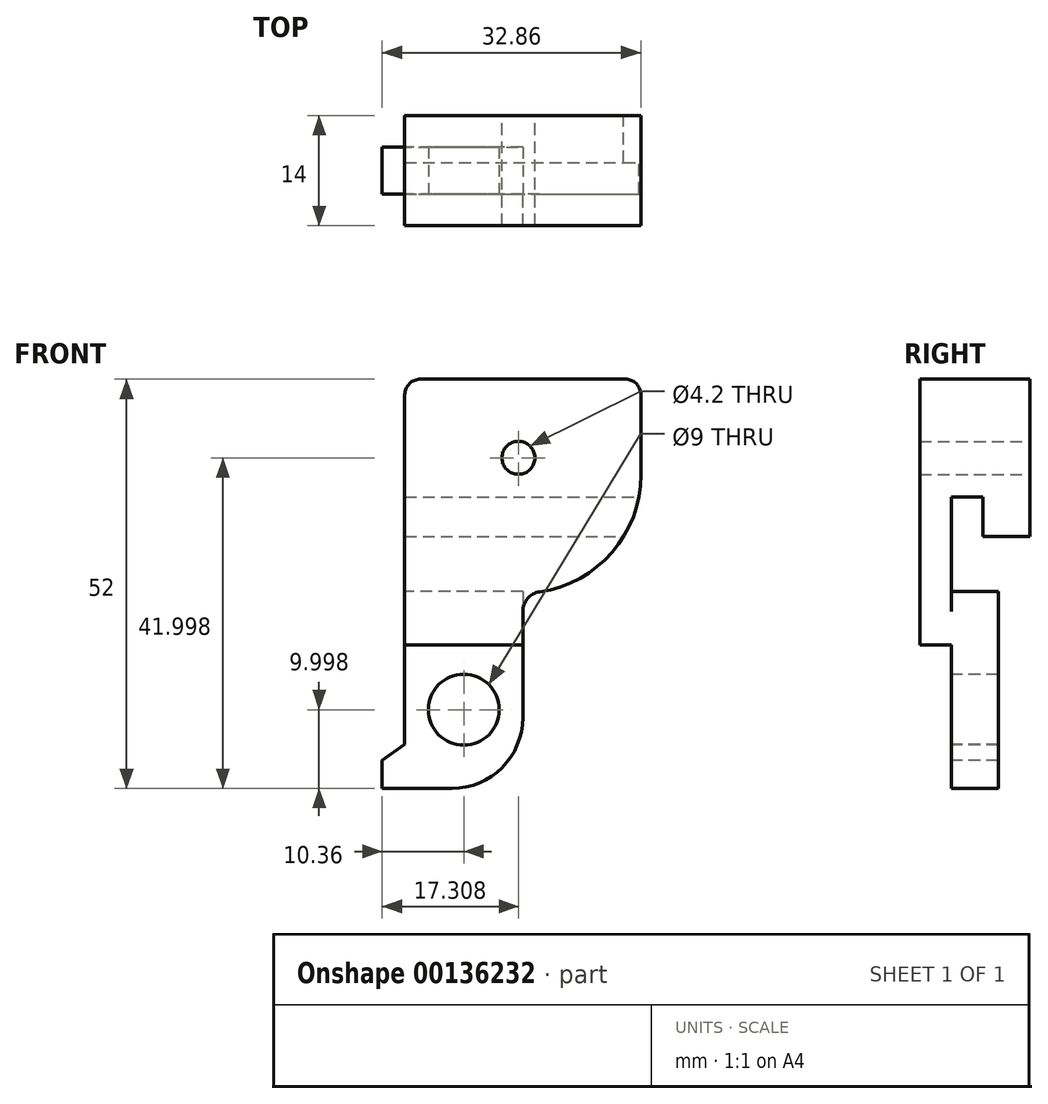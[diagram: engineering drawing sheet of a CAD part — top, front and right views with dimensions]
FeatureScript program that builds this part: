
annotation { "Feature Type Name" : "Feature", "Feature Type Description" : "" }
export const myFeature = defineFeature(function(context is Context, id is Id, definition is map)
    precondition{}
    {
        {
            var Q0;
            Q0=qCreatedBy(makeId("Front.planeOp"),FACE);
            var sketch = newSketch(context, id + "F0", { "sketchPlane" : qUnion([Q0])});
            skLineSegment(sketch, "E0.bottom", {"start": v(-22.02, 18.76) * mm, "end": v(7.98, 18.76) * mm});
            skLineSegment(sketch, "E0.top", {"start": v(-7.02, -8.24) * mm, "end": v(7.98, -8.24) * mm});
            skLineSegment(sketch, "E0.left", {"start": v(-22.02, 18.76) * mm, "end": v(-22.02, -8.24) * mm});
            skLineSegment(sketch, "E0.right", {"start": v(7.98, 18.76) * mm, "end": v(7.98, -8.24) * mm});
            skLineSegment(sketch, "E1.bottom", {"start": v(-22.02, 13.76) * mm, "end": v(7.98, 13.76) * mm});
            skLineSegment(sketch, "E1.top", {"start": v(-22.02, 3.76) * mm, "end": v(7.98, 3.76) * mm});
            skLineSegment(sketch, "E1.left", {"start": v(-22.02, 13.76) * mm, "end": v(-22.02, 3.76) * mm});
            skLineSegment(sketch, "E1.right", {"start": v(7.98, 13.76) * mm, "end": v(7.98, 3.76) * mm});
            skLineSegment(sketch, "E2.bottom", {"start": v(-22.02, 3.76) * mm, "end": v(-7.02, 3.76) * mm});
            skLineSegment(sketch, "E2.top", {"start": v(-22.02, -33.24) * mm, "end": v(-7.02, -33.24) * mm});
            skLineSegment(sketch, "E2.left", {"start": v(-22.02, 3.76) * mm, "end": v(-22.02, -33.24) * mm});
            skLineSegment(sketch, "E2.right", {"start": v(-7.02, -8.24) * mm, "end": v(-7.02, -33.24) * mm});
            skCircle(sketch, "E3", {"center": v(-7.57, 8.76) * mm, "radius": 2.1 * mm});
            skCircle(sketch, "E4", {"center": v(-14.52, -23.24) * mm, "radius": 4.5 * mm});
            skLineSegment(sketch, "E5", {"start": v(-7.02, -8.24) * mm, "end": v(-22.02, -8.24) * mm});
            skLineSegment(sketch, "E6", {"start": v(-7.02, -15) * mm, "end": v(-22.02, -15) * mm});
            skLineSegment(sketch, "E7", {"start": v(-22.02, -33.24) * mm, "end": v(-24.88, -33.24) * mm});
            skLineSegment(sketch, "E8", {"start": v(-24.88, -33.24) * mm, "end": v(-24.88, -29.67) * mm});
            skLineSegment(sketch, "E9", {"start": v(-24.88, -29.67) * mm, "end": v(-22.02, -27.65) * mm});
            skSolve(sketch);
        }
        {
            var Q0;
            {var subQ0=sQuery(id+"F0.wireOp",EDGE,"E0.bottom");Q0=makeQuery(id+"F0.imprint","IMPRINT",FACE,{"disambiguationData":[TD([[makeQuery(id+"F0.imprint","IMPRINT",EDGE,{"derivedFrom":subQ0}),-1.0]])]});}
            var Q1;
            Q1=makeQuery(id+"F0.imprint","IMPRINT",FACE,{"disambiguationData":[TD([[makeQuery(id+"F0.imprint","IMPRINT",EDGE,{"derivedFrom":sQuery(id+"F0.wireOp",EDGE,"E1.bottom")}),-1.0]])]});
            var Q2;
            {var subQ3=sQuery(id+"F0.wireOp",EDGE,"E0.top");Q2=makeQuery(id+"F0.imprint","IMPRINT",FACE,{"disambiguationData":[TD([[makeQuery(id+"F0.imprint","IMPRINT",EDGE,{"derivedFrom":subQ3}),1.0]])]});}
            var Q3;
            {var subQ0=sQuery(id+"F0.wireOp",EDGE,"E5");Q3=makeQuery(id+"F0.imprint","IMPRINT",FACE,{"disambiguationData":[TD([[makeQuery(id+"F0.imprint","IMPRINT",EDGE,{"derivedFrom":subQ0}),1.0]])]});}
            extrude(context, id + "F1", {"entities" : qUnion([Q0, Q1, Q2, Q3]), "depth" : 4 * mm});
        }
        {
            var Q0;
            Q0=makeQuery(id+"F0.imprint","IMPRINT",FACE,{"disambiguationData":[TD([[makeQuery(id+"F0.imprint","IMPRINT",EDGE,{"derivedFrom":sQuery(id+"F0.wireOp",EDGE,"E1.bottom")}),-1.0]])]});
            extrude(context, id + "F2", {"entities" : qUnion([Q0]), "operationType" : NewBodyOperationType.ADD, "oppositeDirection" : true, "depth" : 4 * mm});
        }
        {
            var Q0;
            Q0=makeQuery(id+"F2.opExtrude","CAP_FACE",FACE,{"disambiguationData":[OSD([sQuery(id+"F0.wireOp",EDGE,"E1.bottom"),sQuery(id+"F0.wireOp",EDGE,"E1.top"),sQuery(id+"F0.wireOp",EDGE,"E1.left"),sQuery(id+"F0.wireOp",EDGE,"E1.right"),sQuery(id+"F0.wireOp",EDGE,"E2.bottom"),sQuery(id+"F0.wireOp",EDGE,"E3")])],"isStart":false});
            extrude(context, id + "F3", {"entities" : qUnion([Q0]), "depth" : 6 * mm});
        }
        {
            var Q0;
            Q0=makeQuery(id+"F3.opExtrude","SWEPT_FACE",FACE,{"disambiguationData":[OSD([sQuery(id+"F0.wireOp",EDGE,"E1.top"),sQuery(id+"F0.wireOp",EDGE,"E2.bottom")])]});
            extrude(context, id + "F4", {"entities" : qUnion([Q0]), "operationType" : NewBodyOperationType.ADD, "depth" : 5 * mm});
        }
        {
            var Q0;
            {var subQ0=sQuery(id+"F0.wireOp",EDGE,"E5");Q0=makeQuery(id+"F0.imprint","IMPRINT",FACE,{"disambiguationData":[TD([[makeQuery(id+"F0.imprint","IMPRINT",EDGE,{"derivedFrom":subQ0}),1.0]])]});}
            var Q1;
            {var subQ1=sQuery(id+"F0.wireOp",EDGE,"E2.top");Q1=makeQuery(id+"F0.imprint","IMPRINT",FACE,{"disambiguationData":[TD([[makeQuery(id+"F0.imprint","IMPRINT",EDGE,{"derivedFrom":subQ1}),1.0]])]});}
            extrude(context, id + "F5", {"entities" : qUnion([Q0, Q1]), "operationType" : NewBodyOperationType.ADD, "oppositeDirection" : true, "depth" : 6 * mm});
        }
        {
            var Q0;
            Q0=makeQuery(id+"F3.opExtrude","SWEPT_FACE",FACE,{"disambiguationData":[OSD([sQuery(id+"F0.wireOp",EDGE,"E1.bottom")])]});
            extrude(context, id + "F6", {"entities" : qUnion([Q0]), "operationType" : NewBodyOperationType.ADD, "depth" : 5 * mm});
        }
        {
            var Q0;
            Q0=makeQuery(id+"F1.opExtrude","SWEPT_EDGE",EDGE,{"disambiguationData":[OSD([sQuery(id+"F0.wireOp",EDGE,"E0.top"),sQuery(id+"F0.wireOp",EDGE,"E2.right")])]});
            fillet(context, id + "F7", {"entities" : qUnion([Q0]), "radius" : 2.5 * mm, "tangentPropagation" : true, "allowEdgeOverflow" : false});
        }
        {
            var Q0;
            Q0=makeQuery(id+"F1.opExtrude","SWEPT_EDGE",EDGE,{"disambiguationData":[OSD([sQuery(id+"F0.wireOp",EDGE,"E0.top"),sQuery(id+"F0.wireOp",EDGE,"E0.right")])]});
            fillet(context, id + "F8", {"entities" : qUnion([Q0]), "radius" : 15 * mm, "tangentPropagation" : true, "allowEdgeOverflow" : false});
        }
        {
            var Q0;
            {var subQ0=sQuery(id+"F0.wireOp",EDGE,"E7");Q0=makeQuery(id+"F0.imprint","IMPRINT",FACE,{"disambiguationData":[TD([[makeQuery(id+"F0.imprint","IMPRINT",EDGE,{"derivedFrom":subQ0}),-1.0]])]});}
            extrude(context, id + "F9", {"entities" : qUnion([Q0]), "operationType" : NewBodyOperationType.ADD, "oppositeDirection" : true, "depth" : 6 * mm});
        }
        {
            var Q0;
            Q0=makeQuery(id+"F5.opExtrude","SWEPT_EDGE",EDGE,{"disambiguationData":[OSD([sQuery(id+"F0.wireOp",EDGE,"E2.top"),sQuery(id+"F0.wireOp",EDGE,"E2.right")])]});
            fillet(context, id + "F10", {"entities" : qUnion([Q0]), "radius" : 9 * mm, "tangentPropagation" : true, "allowEdgeOverflow" : false});
        }
        {
            var Q0;
            Q0=makeQuery(id+"F1.opExtrude","SWEPT_EDGE",EDGE,{"disambiguationData":[OSD([sQuery(id+"F0.wireOp",EDGE,"E0.bottom"),sQuery(id+"F0.wireOp",EDGE,"E0.left")])]});
            var Q1;
            Q1=makeQuery(id+"F1.opExtrude","SWEPT_EDGE",EDGE,{"disambiguationData":[OSD([sQuery(id+"F0.wireOp",EDGE,"E0.bottom"),sQuery(id+"F0.wireOp",EDGE,"E0.right")])]});
            fillet(context, id + "F11", {"entities" : qUnion([Q0, Q1]), "radius" : 2 * mm, "tangentPropagation" : true, "allowEdgeOverflow" : false});
        }
    });
